# Revit family: tectron-rondo_infra-red-flush-valve-for-urinal_37421000
name_source: partatom
category: Plumbing Fixtures
revit_build: Autodesk Revit 2014 (Build: 20130308_1515(x64)
units: mm (PartAtom-declared; Revit-internal decimal feet)

## types (1)
- tectron-rondo_infra-red-flush-valve-for-urinal_37421000
    ADA Compliant = No
    Assembly Code = C1030220
    AssetType = Fixed
    CW Connection = Yes
    CWFU = 4.5
    ClassificationName = Uniclass 2015
    ClassificationValue = Pr_40_20_96_45
    Cold Water Connection Diameter = 10 mm  [stored 0.0328084 ft]
    Color = Chrome
    Cost = 0 $
    Default Elevation = 600 mm
    Description = Eurosmart Cosmopolitan. Single-lever sink mixer 1/2. medium spout. single hole installation. mousseur. adjustable flow rate limiter. swivel tubular spout. swivel area 140. flexible connection hoses. rapid installation system. Qualitel approval
    DocumentationMaintenance = http://d3unq1hljpybmw.cloudfront.net
    DocumentationTechnical = http://d3unq1hljpybmw.cloudfront.net
    DurationUnit = Years
    Ecojoy = No
    ExpectedLife = 0
    Faucet Material = Grohe-Chrome
    Features = GROHE StarLight® finish. GROHE SilkMove® 35 mm ceramic cartridge with Eco-Override-Stop and cold start function
    Finish = Chrome
    HW Connection = Yes
    HWFU = 4.5
    Hot Water Connection Diameter = 10 mm  [stored 0.0328084 ft]
    Keynote = N13
    Low Emitting Material = No
    Manufacturer = Grohe Limited
    Masterformat Number = 01 52 19
    Masterformat Title = Sanitary Facilities
    Material = Chrome
    Model = Tectron Rondo Infra red Flush - 37421000
    ModelNumber = Tectron Rondo Infra red Flush - 37421000
    NBSDescription = Commercial stainless steel sinks;
    NBSObjectName = Commercial stainless steel sinks;
    NBSReference = 45-35-15/432
    Product Documentation Link = http://www.grohe.com
    Product Page URL = http://www.grohe.com
    ProductionYear = 2016
    Type Comments = Tectron Rondo Infra red Flush - 37421000
    TypeName = Tectron Rondo Infra red Flush - 37421000
    URL = www.grohe.com
    Vent Connection = No
    WFU = 0
    WarrantyDurationUnit = Years
    Waste Connection = No
    _BIMspec_GUID = 0
    _current revision = 1
    _distributed by = www.bimstore.co.uk

note: [stored X ft] marks values corroborated as IEEE doubles in the binary element streams (Revit-internal decimal feet)

## geometry (parser evidence)
native form markers: Blend x6, Sweep x1
no freeform markers — native parametric forms only
